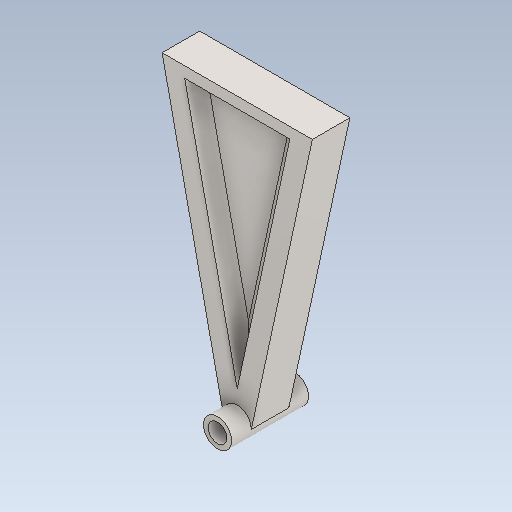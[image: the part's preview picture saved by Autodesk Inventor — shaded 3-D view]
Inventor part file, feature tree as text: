
AUTODESK INVENTOR PART (.ipt)
format: ipt  version: 2021 (Build 250183000, 183)  size: 124,416 bytes
history: mixed  units: mm
features: other x1, fillet x1, imported_body x1
ambient origin geometry x8: Origin, YZ Plane, XZ Plane, XY Plane, X Axis, Y Axis, Z Axis, Center Point
bodies: Body1 (imported_parasolid)
feature tree (3):
  other  "Sólido1"
  fillet  "Fillet1"  [1 undecoded]
  imported_body  NMx_Import_Brep_tag  [imported B-rep: ~17 faces, bbox_mm=[80.0, 150.0, 41.0]]
note: 1 required parameter value undecoded (feature->parameter linkage not recoverable at this tier; creation-order binding heuristic only, values carry confidence <= 0.55)
